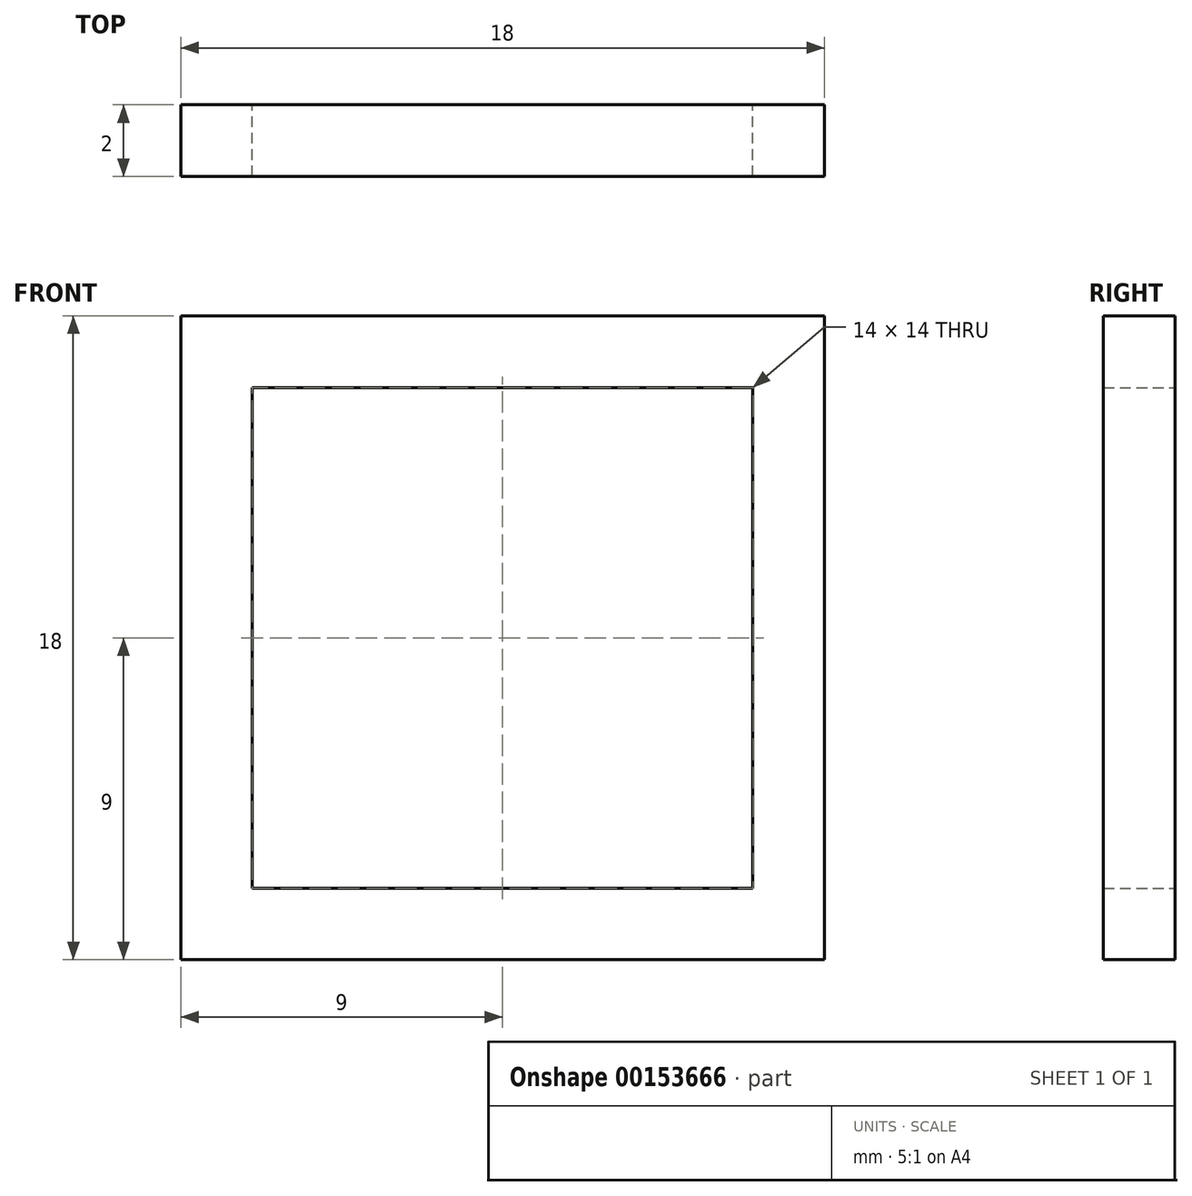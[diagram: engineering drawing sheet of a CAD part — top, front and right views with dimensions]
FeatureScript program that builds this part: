
annotation { "Feature Type Name" : "Feature", "Feature Type Description" : "" }
export const myFeature = defineFeature(function(context is Context, id is Id, definition is map)
    precondition{}
    {
        {
            var Q0;
            Q0=qCreatedBy(makeId("Front.planeOp"),FACE);
            var sketch = newSketch(context, id + "F0", { "sketchPlane" : qUnion([Q0])});
            skLineSegment(sketch, "E0.bottom", {"start": v(9, 9) * mm, "end": v(-9, 9) * mm});
            skLineSegment(sketch, "E0.top", {"start": v(9, -9) * mm, "end": v(-9, -9) * mm});
            skLineSegment(sketch, "E0.left", {"start": v(9, 9) * mm, "end": v(9, -9) * mm});
            skLineSegment(sketch, "E0.right", {"start": v(-9, 9) * mm, "end": v(-9, -9) * mm});
            skPoint(sketch, "E0.middle", {"position": v(0, 0) * mm});
            skLineSegment(sketch, "E1.bottom", {"start": v(7, 7) * mm, "end": v(-7, 7) * mm});
            skLineSegment(sketch, "E1.top", {"start": v(7, -7) * mm, "end": v(-7, -7) * mm});
            skLineSegment(sketch, "E1.left", {"start": v(7, 7) * mm, "end": v(7, -7) * mm});
            skLineSegment(sketch, "E1.right", {"start": v(-7, 7) * mm, "end": v(-7, -7) * mm});
            skSolve(sketch);
        }
        {
            var Q0;
            Q0=makeQuery(id+"F0.imprint","IMPRINT",FACE,{"disambiguationData":[TD([[makeQuery(id+"F0.imprint","IMPRINT",EDGE,{"derivedFrom":sQuery(id+"F0.wireOp",EDGE,"E0.bottom")}),1.0]])]});
            extrude(context, id + "F1", {"entities" : qUnion([Q0]), "depth" : 2 * mm});
        }
    });
